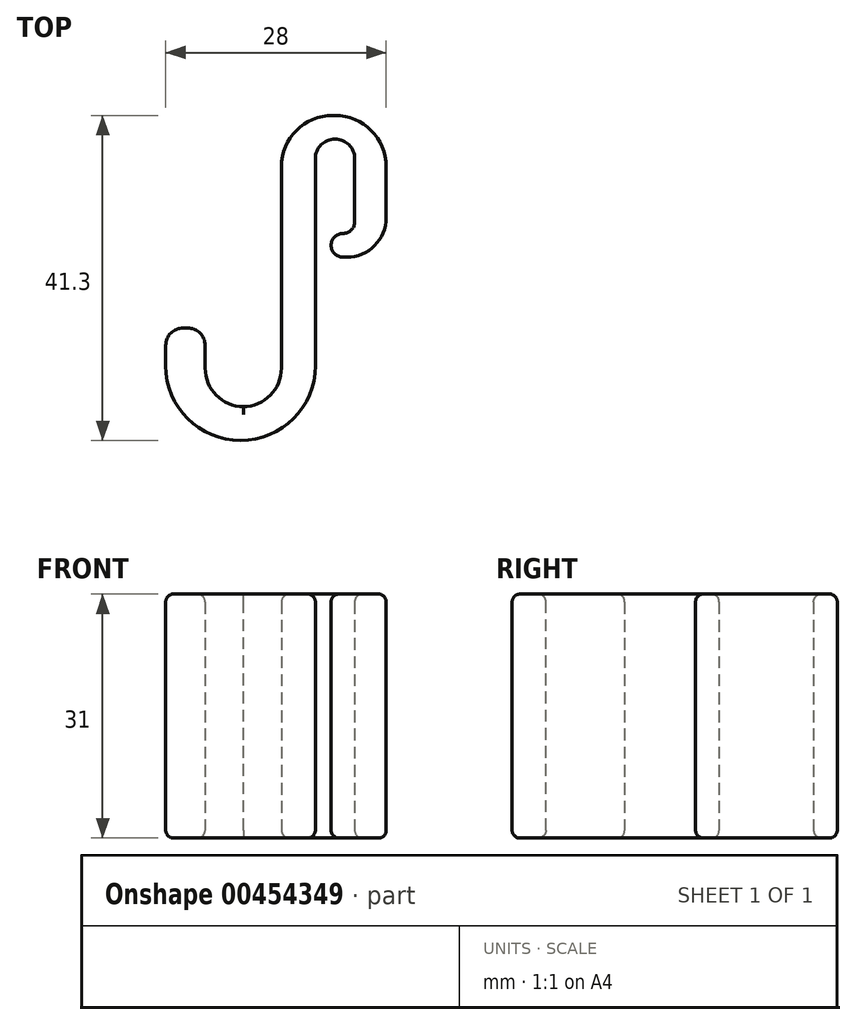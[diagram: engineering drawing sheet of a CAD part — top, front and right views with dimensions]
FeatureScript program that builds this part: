
annotation { "Feature Type Name" : "Feature", "Feature Type Description" : "" }
export const myFeature = defineFeature(function(context is Context, id is Id, definition is map)
    precondition{}
    {
        {
            var Q0;
            Q0=qCreatedBy(makeId("Top.planeOp"),FACE);
            var sketch = newSketch(context, id + "F0", { "sketchPlane" : qUnion([Q0])});
            skLineSegment(sketch, "E0", {"start": v(-25.14, 15.47) * mm, "end": v(-25.14, 52.47) * mm});
            skLineSegment(sketch, "E1", {"start": v(-25.14, 52.47) * mm, "end": v(-11.84, 52.47) * mm});
            skLineSegment(sketch, "E2", {"start": v(-11.84, 52.47) * mm, "end": v(-11.84, 34.47) * mm});
            skLineSegment(sketch, "E3", {"start": v(-25.14, 15.47) * mm, "end": v(-34.84, 15.47) * mm});
            skLineSegment(sketch, "E4", {"start": v(-34.84, 15.47) * mm, "end": v(-34.84, 25.47) * mm});
            skLineSegment(sketch, "E5", {"start": v(-34.84, 25.47) * mm, "end": v(-39.84, 25.47) * mm});
            skLineSegment(sketch, "E6", {"start": v(-15.84, 49.47) * mm, "end": v(-15.84, 37.47) * mm});
            skLineSegment(sketch, "E7", {"start": v(-15.84, 37.47) * mm, "end": v(-18.84, 37.47) * mm});
            skLineSegment(sketch, "E8", {"start": v(-11.84, 34.47) * mm, "end": v(-18.84, 34.47) * mm});
            skLineSegment(sketch, "E9", {"start": v(-18.84, 34.47) * mm, "end": v(-18.84, 37.47) * mm});
            skLineSegment(sketch, "E10", {"start": v(-20.84, 49.47) * mm, "end": v(-15.84, 49.47) * mm});
            skLineSegment(sketch, "E11", {"start": v(-20.84, 49.47) * mm, "end": v(-20.84, 11.17) * mm});
            skLineSegment(sketch, "E12", {"start": v(-20.84, 11.17) * mm, "end": v(-39.84, 11.17) * mm});
            skLineSegment(sketch, "E13", {"start": v(-39.84, 11.17) * mm, "end": v(-39.84, 25.47) * mm});
            skSolve(sketch);
        }
        {
            var Q0;
            Q0=makeQuery(id+"F0.imprint","IMPRINT",FACE,{"disambiguationData":[TD([[makeQuery(id+"F0.imprint","IMPRINT",EDGE,{"derivedFrom":sQuery(id+"F0.wireOp",EDGE,"E0")}),-1.0]])]});
            extrude(context, id + "F1", {"entities" : qUnion([Q0]), "depth" : 31 * mm});
        }
        {
            var Q0;
            Q0=makeQuery(id+"F1.opExtrude","SWEPT_EDGE",EDGE,{"disambiguationData":[OSD([sQuery(id+"F0.wireOp",EDGE,"E4"),sQuery(id+"F0.wireOp",EDGE,"E5")])]});
            var Q1;
            Q1=makeQuery(id+"F1.opExtrude","SWEPT_EDGE",EDGE,{"disambiguationData":[OSD([sQuery(id+"F0.wireOp",EDGE,"E5"),sQuery(id+"F0.wireOp",EDGE,"E13")])]});
            fillet(context, id + "F2", {"entities" : qUnion([Q0, Q1]), "radius" : 2.2 * mm, "tangentPropagation" : true, "allowEdgeOverflow" : false});
        }
        {
            var Q0;
            Q0=makeQuery(id+"F1.opExtrude","SWEPT_EDGE",EDGE,{"disambiguationData":[OSD([sQuery(id+"F0.wireOp",EDGE,"E7"),sQuery(id+"F0.wireOp",EDGE,"E9")])]});
            var Q1;
            Q1=makeQuery(id+"F1.opExtrude","SWEPT_EDGE",EDGE,{"disambiguationData":[OSD([sQuery(id+"F0.wireOp",EDGE,"E8"),sQuery(id+"F0.wireOp",EDGE,"E9")])]});
            fillet(context, id + "F3", {"entities" : qUnion([Q0, Q1]), "radius" : 1.5 * mm, "tangentPropagation" : true, "allowEdgeOverflow" : false});
        }
        {
            var Q0;
            Q0=makeQuery(id+"F1.opExtrude","SWEPT_EDGE",EDGE,{"disambiguationData":[OSD([sQuery(id+"F0.wireOp",EDGE,"E0"),sQuery(id+"F0.wireOp",EDGE,"E1")])]});
            var Q1;
            Q1=makeQuery(id+"F1.opExtrude","SWEPT_EDGE",EDGE,{"disambiguationData":[OSD([sQuery(id+"F0.wireOp",EDGE,"E1"),sQuery(id+"F0.wireOp",EDGE,"E2")])]});
            fillet(context, id + "F4", {"entities" : qUnion([Q0, Q1]), "radius" : 6.5 * mm, "tangentPropagation" : true, "allowEdgeOverflow" : false});
        }
        {
            var Q0;
            Q0=makeQuery(id+"F1.opExtrude","SWEPT_EDGE",EDGE,{"disambiguationData":[OSD([sQuery(id+"F0.wireOp",EDGE,"E10"),sQuery(id+"F0.wireOp",EDGE,"E11")])]});
            var Q1;
            Q1=makeQuery(id+"F1.opExtrude","SWEPT_EDGE",EDGE,{"disambiguationData":[OSD([sQuery(id+"F0.wireOp",EDGE,"E6"),sQuery(id+"F0.wireOp",EDGE,"E10")])]});
            fillet(context, id + "F5", {"entities" : qUnion([Q0, Q1]), "radius" : 2.5 * mm, "tangentPropagation" : true, "allowEdgeOverflow" : false});
        }
        {
            var Q0;
            Q0=makeQuery(id+"F1.opExtrude","SWEPT_EDGE",EDGE,{"disambiguationData":[OSD([sQuery(id+"F0.wireOp",EDGE,"E3"),sQuery(id+"F0.wireOp",EDGE,"E4")])]});
            var Q1;
            Q1=makeQuery(id+"F1.opExtrude","SWEPT_EDGE",EDGE,{"disambiguationData":[OSD([sQuery(id+"F0.wireOp",EDGE,"E0"),sQuery(id+"F0.wireOp",EDGE,"E3")])]});
            fillet(context, id + "F6", {"entities" : qUnion([Q0, Q1]), "radius" : 4.9 * mm, "tangentPropagation" : true, "allowEdgeOverflow" : false});
        }
        {
            var Q0;
            Q0=makeQuery(id+"F1.opExtrude","SWEPT_EDGE",EDGE,{"disambiguationData":[OSD([sQuery(id+"F0.wireOp",EDGE,"E11"),sQuery(id+"F0.wireOp",EDGE,"E12")])]});
            var Q1;
            Q1=makeQuery(id+"F1.opExtrude","SWEPT_EDGE",EDGE,{"disambiguationData":[OSD([sQuery(id+"F0.wireOp",EDGE,"E12"),sQuery(id+"F0.wireOp",EDGE,"E13")])]});
            fillet(context, id + "F7", {"entities" : qUnion([Q0, Q1]), "radius" : 9.5 * mm, "tangentPropagation" : true, "allowEdgeOverflow" : false});
        }
        {
            var Q0;
            Q0=makeQuery(id+"F1.opExtrude","SWEPT_EDGE",EDGE,{"disambiguationData":[OSD([sQuery(id+"F0.wireOp",EDGE,"E6"),sQuery(id+"F0.wireOp",EDGE,"E7")])]});
            fillet(context, id + "F8", {"entities" : qUnion([Q0]), "radius" : 1.5 * mm, "tangentPropagation" : true, "allowEdgeOverflow" : false});
        }
        {
            var Q0;
            Q0=makeQuery(id+"F1.opExtrude","SWEPT_EDGE",EDGE,{"disambiguationData":[OSD([sQuery(id+"F0.wireOp",EDGE,"E2"),sQuery(id+"F0.wireOp",EDGE,"E8")])]});
            fillet(context, id + "F9", {"entities" : qUnion([Q0]), "radius" : 5 * mm, "tangentPropagation" : true, "allowEdgeOverflow" : false});
        }
        {
            var Q0;
            Q0=makeQuery(id+"F1.opExtrude","CAP_FACE",FACE,{"disambiguationData":[OSD([sQuery(id+"F0.wireOp",EDGE,"E0"),sQuery(id+"F0.wireOp",EDGE,"E1"),sQuery(id+"F0.wireOp",EDGE,"E2"),sQuery(id+"F0.wireOp",EDGE,"E3"),sQuery(id+"F0.wireOp",EDGE,"E4"),sQuery(id+"F0.wireOp",EDGE,"E5"),sQuery(id+"F0.wireOp",EDGE,"E6"),sQuery(id+"F0.wireOp",EDGE,"E7"),sQuery(id+"F0.wireOp",EDGE,"E8"),sQuery(id+"F0.wireOp",EDGE,"E9"),sQuery(id+"F0.wireOp",EDGE,"E10"),sQuery(id+"F0.wireOp",EDGE,"E11"),sQuery(id+"F0.wireOp",EDGE,"E12"),sQuery(id+"F0.wireOp",EDGE,"E13")])],"isStart":true});
            var Q1;
            Q1=makeQuery(id+"F1.opExtrude","CAP_FACE",FACE,{"disambiguationData":[OSD([sQuery(id+"F0.wireOp",EDGE,"E0"),sQuery(id+"F0.wireOp",EDGE,"E1"),sQuery(id+"F0.wireOp",EDGE,"E2"),sQuery(id+"F0.wireOp",EDGE,"E3"),sQuery(id+"F0.wireOp",EDGE,"E4"),sQuery(id+"F0.wireOp",EDGE,"E5"),sQuery(id+"F0.wireOp",EDGE,"E6"),sQuery(id+"F0.wireOp",EDGE,"E7"),sQuery(id+"F0.wireOp",EDGE,"E8"),sQuery(id+"F0.wireOp",EDGE,"E9"),sQuery(id+"F0.wireOp",EDGE,"E10"),sQuery(id+"F0.wireOp",EDGE,"E11"),sQuery(id+"F0.wireOp",EDGE,"E12"),sQuery(id+"F0.wireOp",EDGE,"E13")])],"isStart":false});
            fillet(context, id + "F10", {"entities" : qUnion([Q0, Q1]), "radius" : 1 * mm, "tangentPropagation" : true, "allowEdgeOverflow" : false});
        }
    });
